# Revit family: Deca_Misturador Bidê Aspen_1895.C35
name_source: partatom
category: Plumbing Fixtures
revit_build: Autodesk Revit Architecture 2012 (Build: 20110916_2132(x64)
units: mm (PartAtom-declared; Revit-internal decimal feet)

## types (1)
- 1895.C35_Cromado CR10
    Acompanha o Produto = Válvula de escoamento 1602.C.PLA
    Aprovado por = Contino/quattroD
    Assembly Code = D2020
    Atendimento ao Cliente = 0800-0117073
    CWFU = 0
    Consumo = Varia com a pressão
    Criado por = Contino/quattroD
    Código = 1895.C35
    Default Elevation = 0 mm  [stored 0 ft]
    Description = Misturador bidê
    Diâmetro Água Fria = 15 mm  [stored 0.0492126 ft]
    Diâmetro Água Quente = 15 mm  [stored 0.0492126 ft]
    Flow Pressure = 0.00 psi
    HWFU = 0
    Informações Complementares = Mecanismo: 3 1/2 de volta
    Linha = Aspen
    Louça/Metais = Metal
    Manufacturer = Deca
    Material = Deca_Latão Cromado e Plástico de Engenharia
    Misturador = Deca CR10 Cromado Metal
    Model = 1895.C35
    Norma = ABNT NBR 14390: 2001
    Peso Liquido (Kg) = 1.79
    Pressão = 2 A 40 mca
    Produto = Misturador bidê
    Raio Água Fria = 8 mm  [stored 0.0262467 ft]
    Raio Água Quente = 8 mm  [stored 0.0262467 ft]
    Segmento = Competitivo
    URL = www.deca.com.br/produtos
    Variações de COR = Cromado (1895.C35)
    Vendido Separadamente = Ligação Flexível: 30 cm (4607.C.030), 40 cm (4607.C.040), 50 cm (4607.C.050).
    WFU = 0

note: [stored X ft] marks values corroborated as IEEE doubles in the binary element streams (Revit-internal decimal feet)

## geometry (parser evidence)
native form markers: Blend x4, Sweep x4
no freeform markers — native parametric forms only
